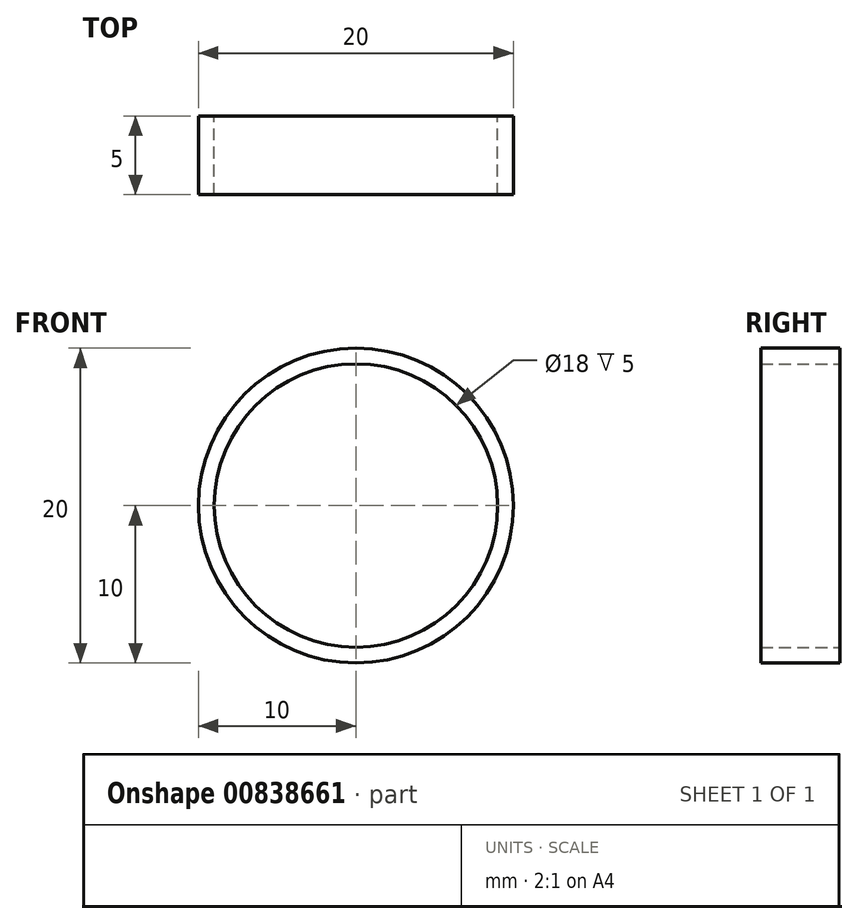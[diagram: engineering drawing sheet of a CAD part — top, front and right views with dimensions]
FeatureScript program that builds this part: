
annotation { "Feature Type Name" : "Feature", "Feature Type Description" : "" }
export const myFeature = defineFeature(function(context is Context, id is Id, definition is map)
    precondition{}
    {
        {
            var Q0;
            Q0=qCreatedBy(makeId("Front.planeOp"),FACE);
            var sketch = newSketch(context, id + "F0", { "sketchPlane" : qUnion([Q0])});
            skCircle(sketch, "E0", {"center": v(0, 0) * mm, "radius": 10 * mm});
            skCircle(sketch, "E1", {"center": v(0, 0) * mm, "radius": 9 * mm});
            skSolve(sketch);
        }
        {
            var Q0;
            Q0 = qSketchRegion(id + "F0", true);
            extrude(context, id + "F1", {"entities" : qUnion([Q0]), "depth" : 5 * mm, "offsetDistance" : 25 * mm});
        }
    });
